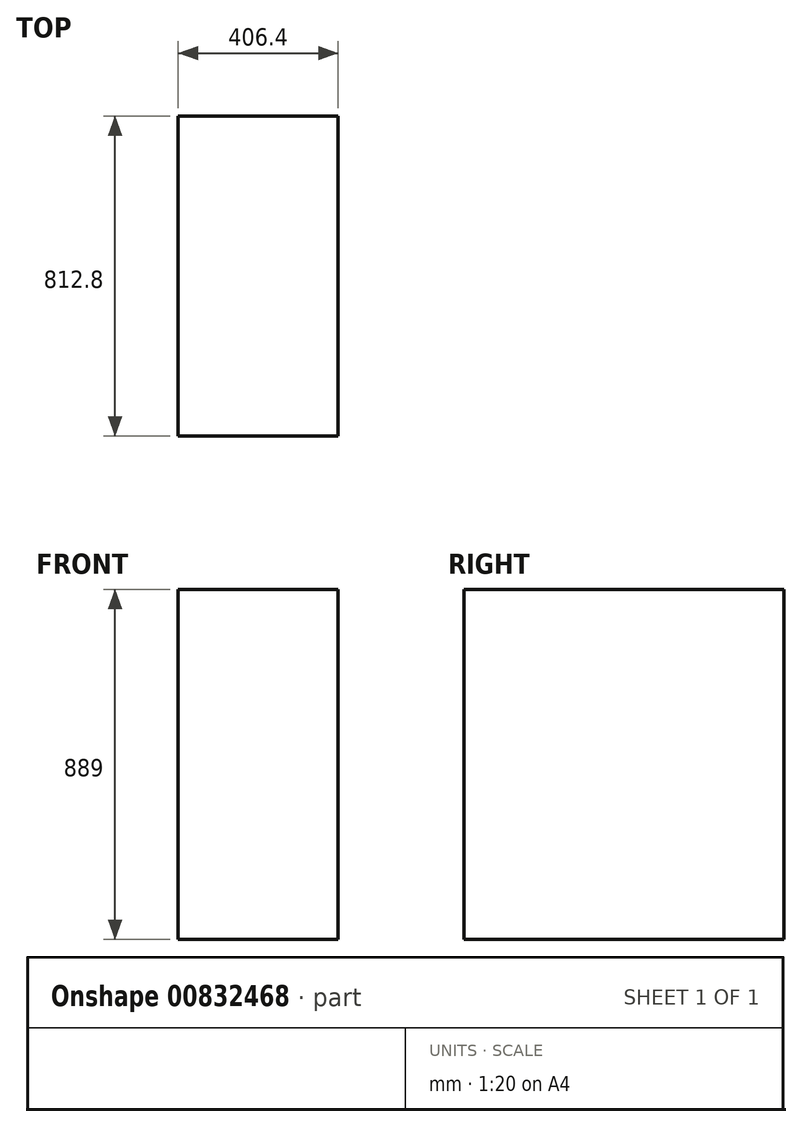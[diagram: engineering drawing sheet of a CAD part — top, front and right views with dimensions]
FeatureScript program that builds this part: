
annotation { "Feature Type Name" : "Feature", "Feature Type Description" : "" }
export const myFeature = defineFeature(function(context is Context, id is Id, definition is map)
    precondition{}
    {
        {
            var Q0;
            Q0=qCreatedBy(makeId("Top.planeOp"),FACE);
            var sketch = newSketch(context, id + "F0", { "sketchPlane" : qUnion([Q0])});
            skLineSegment(sketch, "E0.bottom", {"start": v(0, 0) * mm, "end": v(406.4, 0) * mm});
            skLineSegment(sketch, "E0.top", {"start": v(0, 812.8) * mm, "end": v(406.4, 812.8) * mm});
            skLineSegment(sketch, "E0.left", {"start": v(0, 0) * mm, "end": v(0, 812.8) * mm});
            skLineSegment(sketch, "E0.right", {"start": v(406.4, 0) * mm, "end": v(406.4, 812.8) * mm});
            skSolve(sketch);
        }
        {
            var Q0;
            Q0 = qSketchRegion(id + "F0", true);
            extrude(context, id + "F1", {"entities" : qUnion([Q0]), "depth" : 889 * mm, "offsetDistance" : 25.4 * mm});
        }
    });
